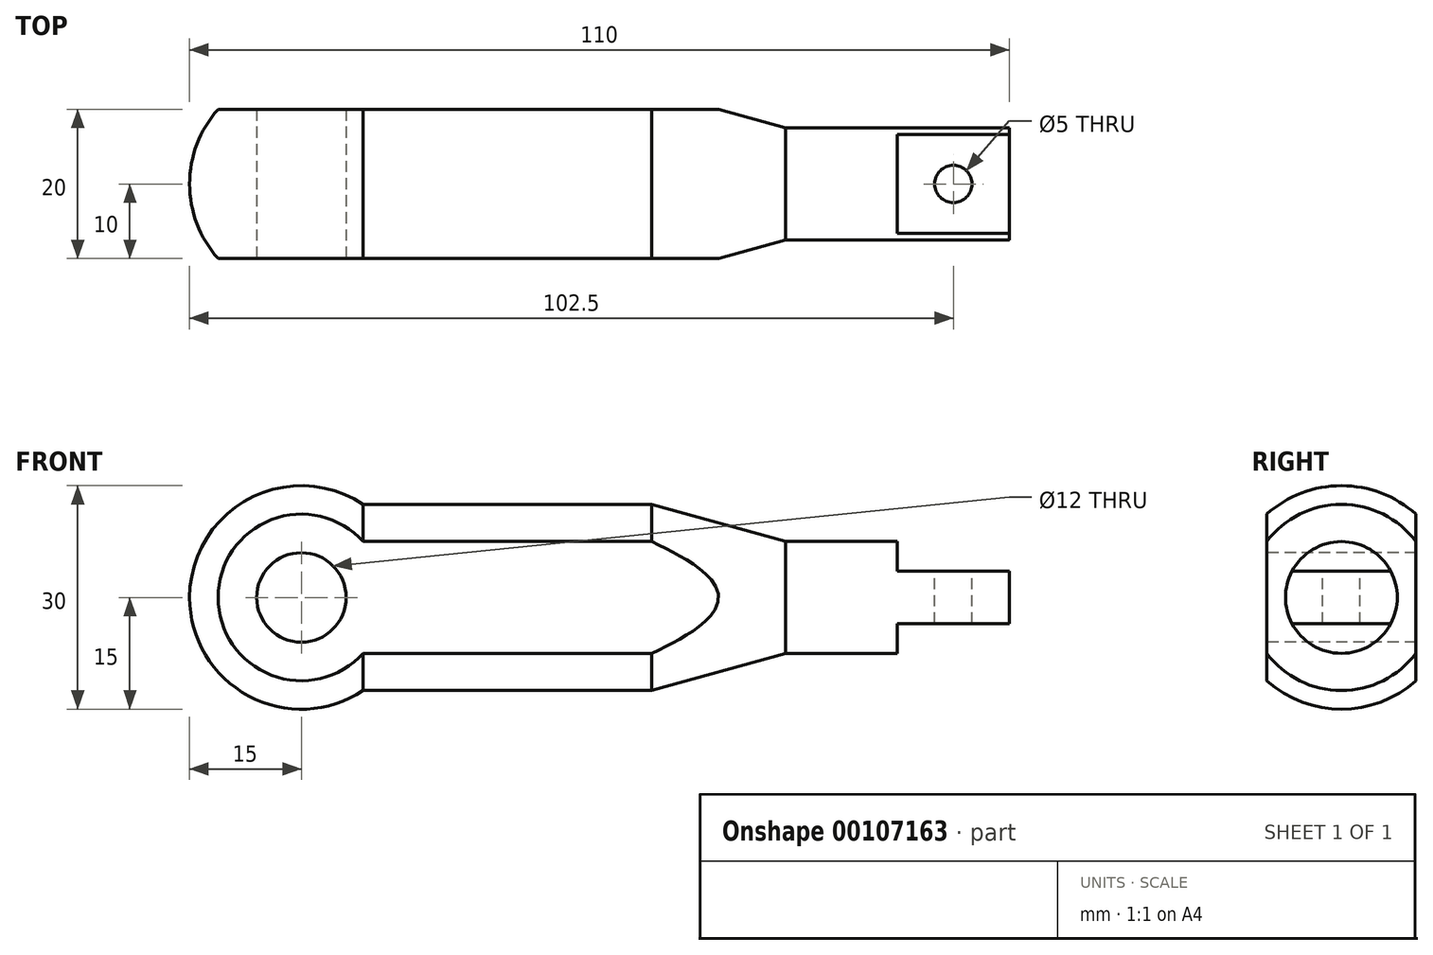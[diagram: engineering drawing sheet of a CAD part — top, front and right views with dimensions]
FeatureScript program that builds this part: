
annotation { "Feature Type Name" : "Feature", "Feature Type Description" : "" }
export const myFeature = defineFeature(function(context is Context, id is Id, definition is map)
    precondition{}
    {
        {
            var Q0;
            Q0=qCreatedBy(makeId("Front.planeOp"),FACE);
            var sketch = newSketch(context, id + "F0", { "sketchPlane" : qUnion([Q0])});
            skArc(sketch, "E0", {"start": v(8.3, 12.5) * mm, "mid": v(-7.1, 13.22) * mm, "end": v(-15, 0) * mm});
            skLineSegment(sketch, "E1", {"start": v(47, 0) * mm, "end": v(47, 12.5) * mm, "construction": true});
            skLineSegment(sketch, "E2", {"start": v(47, 12.5) * mm, "end": v(8.3, 12.5) * mm});
            skLineSegment(sketch, "E3", {"start": v(-15, 0) * mm, "end": v(0, 0) * mm});
            skPoint(sketch, "E4.orphan", {"position": v(-28.76, 0) * mm});
            skLineSegment(sketch, "E5", {"start": v(47, 0) * mm, "end": v(65, 0) * mm, "construction": true});
            skLineSegment(sketch, "E6", {"start": v(65, 0) * mm, "end": v(65, 7.5) * mm, "construction": true});
            skLineSegment(sketch, "E7", {"start": v(47, 12.5) * mm, "end": v(65, 7.5) * mm});
            skLineSegment(sketch, "E8", {"start": v(65, 7.5) * mm, "end": v(95, 7.5) * mm});
            skLineSegment(sketch, "E9", {"start": v(95, 7.5) * mm, "end": v(95, 0) * mm});
            skLineSegment(sketch, "E10", {"start": v(95, 0) * mm, "end": v(0, 0) * mm});
            skSolve(sketch);
        }
        {
            var Q0;
            Q0=makeQuery(id+"F0.imprint","IMPRINT",FACE,{"disambiguationData":[TD([[makeQuery(id+"F0.imprint","IMPRINT",EDGE,{"derivedFrom":sQuery(id+"F0.wireOp",EDGE,"E0")}),1.0]])]});
            var Q1;
            Q1=sQuery(id+"F0.wireOp",EDGE,"E10");
            revolve(context, id + "F1", {"entities" : qUnion([Q0]), "axis" : qUnion([Q1]), "revolveType" : RevolveType.FULL});
        }
        {
            var Q0;
            Q0=qCreatedBy(makeId("Front.planeOp"),FACE);
            var sketch = newSketch(context, id + "F2", { "sketchPlane" : qUnion([Q0])});
            skCircle(sketch, "E11", {"center": v(0, 0) * mm, "radius": 6 * mm});
            skSolve(sketch);
        }
        {
            var Q0;
            Q0 = qSketchRegion(id + "F2", true);
            extrude(context, id + "F3", {"entities" : qUnion([Q0]), "operationType" : NewBodyOperationType.REMOVE, "endBound" : BoundingType.SYMMETRIC, "oppositeDirection" : true, "depth" : 50 * mm});
        }
        {
            var Q0;
            Q0=qCreatedBy(makeId("Top.planeOp"),FACE);
            var sketch = newSketch(context, id + "F4", { "sketchPlane" : qUnion([Q0])});
            skLineSegment(sketch, "E12", {"start": v(0, 0) * mm, "end": v(0, 10) * mm, "construction": true});
            skLineSegment(sketch, "E13", {"start": v(0, 10) * mm, "end": v(0, -10) * mm, "construction": true});
            skLineSegment(sketch, "E14", {"start": v(0, -10) * mm, "end": v(-20, -10) * mm});
            skLineSegment(sketch, "E15", {"start": v(-20, -10) * mm, "end": v(-20, 10) * mm});
            skLineSegment(sketch, "E16", {"start": v(-20, 10) * mm, "end": v(100, 10) * mm});
            skLineSegment(sketch, "E17", {"start": v(100, 10) * mm, "end": v(100, -10) * mm});
            skLineSegment(sketch, "E18", {"start": v(100, -10) * mm, "end": v(0, -10) * mm});
            skSolve(sketch);
        }
        {
            var Q0;
            Q0=makeQuery(id+"F4.imprint","IMPRINT",FACE,{"disambiguationData":[TD([[makeQuery(id+"F4.imprint","IMPRINT",EDGE,{"derivedFrom":sQuery(id+"F4.wireOp",EDGE,"E14")}),-1.0]])]});
            extrude(context, id + "F5", {"entities" : qUnion([Q0]), "operationType" : NewBodyOperationType.INTERSECT, "endBound" : BoundingType.SYMMETRIC, "depth" : 50 * mm});
        }
        {
            var Q0;
            Q0=qCreatedBy(makeId("Front.planeOp"),FACE);
            var sketch = newSketch(context, id + "F6", { "sketchPlane" : qUnion([Q0])});
            skLineSegment(sketch, "E19", {"start": v(0, 0) * mm, "end": v(80, 0) * mm, "construction": true});
            skLineSegment(sketch, "E20", {"start": v(80, 0) * mm, "end": v(80, 3.5) * mm, "construction": true});
            skLineSegment(sketch, "E21", {"start": v(80, 3.5) * mm, "end": v(80, -3.5) * mm, "construction": true});
            skLineSegment(sketch, "E22", {"start": v(80, -8.5) * mm, "end": v(95, -8.5) * mm});
            skLineSegment(sketch, "E23", {"start": v(95, -8.5) * mm, "end": v(95, -3.5) * mm});
            skLineSegment(sketch, "E24", {"start": v(95, -3.5) * mm, "end": v(80, -3.5) * mm});
            skLineSegment(sketch, "E25", {"start": v(80, -3.5) * mm, "end": v(80, -8.5) * mm});
            skLineSegment(sketch, "E26.MirrorCS", {"start": v(80, 8.5) * mm, "end": v(95, 8.5) * mm});
            skLineSegment(sketch, "E27.MirrorCS", {"start": v(80, 3.5) * mm, "end": v(80, 8.5) * mm});
            skLineSegment(sketch, "E28.MirrorCS", {"start": v(95, 3.5) * mm, "end": v(80, 3.5) * mm});
            skLineSegment(sketch, "E29.MirrorCS", {"start": v(95, 8.5) * mm, "end": v(95, 3.5) * mm});
            skSolve(sketch);
        }
        {
            var Q0;
            Q0 = qSketchRegion(id + "F6", true);
            extrude(context, id + "F7", {"entities" : qUnion([Q0]), "operationType" : NewBodyOperationType.REMOVE, "endBound" : BoundingType.SYMMETRIC, "depth" : 25 * mm});
        }
        {
            var Q0;
            Q0=qCreatedBy(makeId("Top.planeOp"),FACE);
            var sketch = newSketch(context, id + "F8", { "sketchPlane" : qUnion([Q0])});
            skLineSegment(sketch, "E30", {"start": v(0, 0) * mm, "end": v(87.5, 0) * mm, "construction": true});
            skCircle(sketch, "E31", {"center": v(87.5, 0) * mm, "radius": 2.5 * mm});
            skSolve(sketch);
        }
        {
            var Q0;
            Q0 = qSketchRegion(id + "F8", true);
            extrude(context, id + "F9", {"entities" : qUnion([Q0]), "operationType" : NewBodyOperationType.REMOVE, "endBound" : BoundingType.SYMMETRIC, "oppositeDirection" : true, "depth" : 25 * mm});
        }
    });
